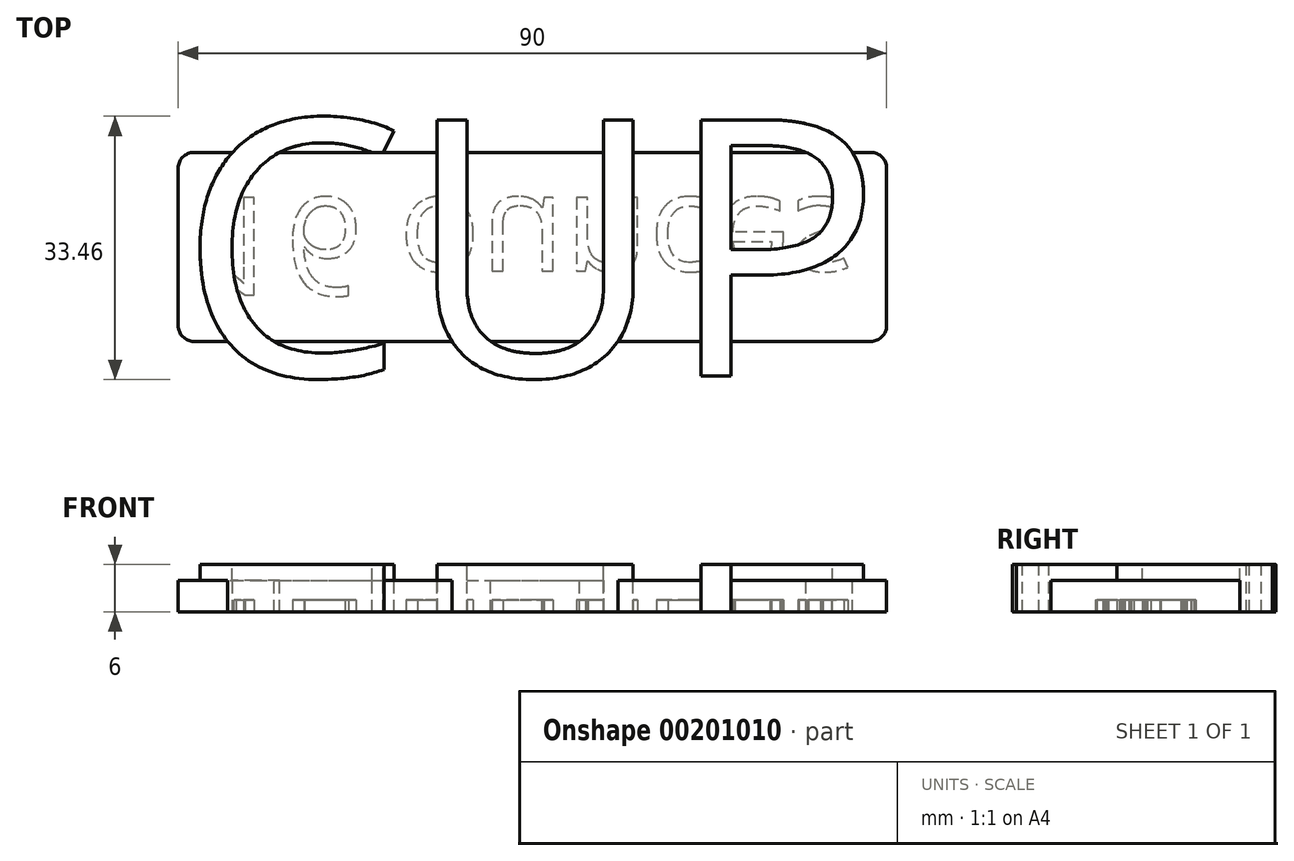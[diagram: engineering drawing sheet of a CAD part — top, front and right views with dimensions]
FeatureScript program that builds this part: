
annotation { "Feature Type Name" : "Feature", "Feature Type Description" : "" }
export const myFeature = defineFeature(function(context is Context, id is Id, definition is map)
    precondition{}
    {
        {
            var Q0;
            Q0=qCreatedBy(makeId("Top.planeOp"),FACE);
            var sketch = newSketch(context, id + "F0", { "sketchPlane" : qUnion([Q0])});
            skLineSegment(sketch, "E0.bottom", {"start": v(-45, 12) * mm, "end": v(45, 12) * mm});
            skLineSegment(sketch, "E0.top", {"start": v(-45, -12) * mm, "end": v(45, -12) * mm});
            skLineSegment(sketch, "E0.left", {"start": v(-45, 12) * mm, "end": v(-45, -12) * mm});
            skLineSegment(sketch, "E0.right", {"start": v(45, 12) * mm, "end": v(45, -12) * mm});
            skLineSegment(sketch, "E1", {"start": v(0, -12) * mm, "end": v(0, 12) * mm, "construction": true});
            skSolve(sketch);
        }
        {
            var Q0;
            Q0=makeQuery(id+"F0.imprint","IMPRINT",FACE,{"disambiguationData":[TD([[makeQuery(id+"F0.imprint","IMPRINT",EDGE,{"derivedFrom":sQuery(id+"F0.wireOp",EDGE,"E0.bottom")}),-1.0]])]});
            extrude(context, id + "F1", {"entities" : qUnion([Q0]), "depth" : 4 * mm});
        }
        {
            var Q0;
            Q0=makeQuery(id+"F1.opExtrude","SWEPT_EDGE",EDGE,{"disambiguationData":[OSD([sQuery(id+"F0.wireOp",EDGE,"E0.top"),sQuery(id+"F0.wireOp",EDGE,"E0.left")])]});
            var Q1;
            Q1=makeQuery(id+"F1.opExtrude","SWEPT_EDGE",EDGE,{"disambiguationData":[OSD([sQuery(id+"F0.wireOp",EDGE,"E0.bottom"),sQuery(id+"F0.wireOp",EDGE,"E0.right")])]});
            var Q2;
            Q2=makeQuery(id+"F1.opExtrude","SWEPT_EDGE",EDGE,{"disambiguationData":[OSD([sQuery(id+"F0.wireOp",EDGE,"E0.bottom"),sQuery(id+"F0.wireOp",EDGE,"E0.left")])]});
            var Q3;
            Q3=makeQuery(id+"F1.opExtrude","SWEPT_EDGE",EDGE,{"disambiguationData":[OSD([sQuery(id+"F0.wireOp",EDGE,"E0.top"),sQuery(id+"F0.wireOp",EDGE,"E0.right")])]});
            fillet(context, id + "F2", {"entities" : qUnion([Q0, Q1, Q2, Q3]), "radius" : 2 * mm, "tangentPropagation" : true, "allowEdgeOverflow" : false});
        }
        {
            var Q0;
            Q0=makeQuery(id+"F1.opExtrude","CAP_FACE",FACE,{"disambiguationData":[OSD([sQuery(id+"F0.wireOp",EDGE,"E0.bottom"),sQuery(id+"F0.wireOp",EDGE,"E0.top"),sQuery(id+"F0.wireOp",EDGE,"E0.left"),sQuery(id+"F0.wireOp",EDGE,"E0.right")])],"isStart":false});
            var sketch = newSketch(context, id + "F3", { "sketchPlane" : qUnion([Q0])});
            skText(sketch, "E2", { "text": "CUP", "fontName": "OpenSans-Regular.ttf"});
            const initialGuessF3  = {"E2": [-0.045, -0.0164, 1, 0, 0.03282]};
            skSetInitialGuess(sketch, initialGuessF3);
            skSolve(sketch);
        }
        {
            var Q0;
            Q0=makeQuery(id+"F1.opExtrude","CAP_FACE",FACE,{"disambiguationData":[OSD([sQuery(id+"F0.wireOp",EDGE,"E0.bottom"),sQuery(id+"F0.wireOp",EDGE,"E0.top"),sQuery(id+"F0.wireOp",EDGE,"E0.left"),sQuery(id+"F0.wireOp",EDGE,"E0.right")])],"isStart":true});
            var sketch = newSketch(context, id + "F4", { "sketchPlane" : qUnion([Q0])});
            skText(sketch, "E3", { "text": "16 ounces", "fontName": "OpenSans-Regular.ttf"});
            const initialGuessF4  = {"E3": [-0.04139, -0.00625, 1, 0, 0.0125]};
            skSetInitialGuess(sketch, initialGuessF4);
            skSolve(sketch);
        }
        {
            var Q0;
            Q0=makeQuery(id+"F4.imprint","IMPRINT",FACE,{"disambiguationData":[TD([[makeQuery(id+"F4.imprint","IMPRINT",EDGE,{"derivedFrom":sQuery(id+"F4.wireOp",EDGE,"E3.sketch_text.stroke-141")}),-1.0]])]});
            var Q1;
            Q1=makeQuery(id+"F4.imprint","IMPRINT",FACE,{"disambiguationData":[TD([[makeQuery(id+"F4.imprint","IMPRINT",EDGE,{"derivedFrom":sQuery(id+"F4.wireOp",EDGE,"E3.sketch_text.stroke-122")}),-1.0]])]});
            var Q2;
            Q2=makeQuery(id+"F4.imprint","IMPRINT",FACE,{"disambiguationData":[TD([[makeQuery(id+"F4.imprint","IMPRINT",EDGE,{"derivedFrom":sQuery(id+"F4.wireOp",EDGE,"E3.sketch_text.stroke-103")}),-1.0]])]});
            var Q3;
            Q3=makeQuery(id+"F4.imprint","IMPRINT",FACE,{"disambiguationData":[TD([[makeQuery(id+"F4.imprint","IMPRINT",EDGE,{"derivedFrom":sQuery(id+"F4.wireOp",EDGE,"E3.sketch_text.stroke-86")}),-1.0]])]});
            var Q4;
            Q4=makeQuery(id+"F4.imprint","IMPRINT",FACE,{"disambiguationData":[TD([[makeQuery(id+"F4.imprint","IMPRINT",EDGE,{"derivedFrom":sQuery(id+"F4.wireOp",EDGE,"E3.sketch_text.stroke-70")}),-1.0]])]});
            var Q5;
            Q5=makeQuery(id+"F4.imprint","IMPRINT",FACE,{"disambiguationData":[TD([[makeQuery(id+"F4.imprint","IMPRINT",EDGE,{"derivedFrom":sQuery(id+"F4.wireOp",EDGE,"E3.sketch_text.stroke-39")}),-1.0]])]});
            var Q6;
            Q6=makeQuery(id+"F4.imprint","IMPRINT",FACE,{"disambiguationData":[TD([[makeQuery(id+"F4.imprint","IMPRINT",EDGE,{"derivedFrom":sQuery(id+"F4.wireOp",EDGE,"E3.sketch_text.stroke-19")}),-1.0]])]});
            var Q7;
            Q7=makeQuery(id+"F4.imprint","IMPRINT",FACE,{"disambiguationData":[TD([[makeQuery(id+"F4.imprint","IMPRINT",EDGE,{"derivedFrom":sQuery(id+"F4.wireOp",EDGE,"E3.sketch_text.stroke-0")}),-1.0]])]});
            var Q8;
            Q8=makeQuery(id+"F4.imprint","IMPRINT",FACE,{"disambiguationData":[TD([[makeQuery(id+"F4.imprint","IMPRINT",EDGE,{"derivedFrom":sQuery(id+"F4.wireOp",EDGE,"E3.sketch_text.stroke-51")}),-1.0]])]});
            extrude(context, id + "F5", {"entities" : qUnion([Q0, Q1, Q2, Q3, Q4, Q5, Q6, Q7, Q8]), "operationType" : NewBodyOperationType.REMOVE, "oppositeDirection" : true, "depth" : 1.5 * mm});
        }
        {
            var Q0;
            {var subQ0=sQuery(id+"F3.wireOp",EDGE,"E2.sketch_text.stroke-4");Q0=makeQuery(id+"F3.imprint","IMPRINT",FACE,{"disambiguationData":[TD([[makeQuery(id+"F3.imprint","IMPRINT",EDGE,{"derivedFrom":subQ0}),-1.0]])]});}
            var Q1;
            {var subQ1=sQuery(id+"F3.wireOp",EDGE,"E2.sketch_text.stroke-1");Q1=makeQuery(id+"F3.imprint","IMPRINT",FACE,{"disambiguationData":[TD([[makeQuery(id+"F3.imprint","IMPRINT",EDGE,{"derivedFrom":subQ1}),-1.0]])]});}
            var Q2;
            {var subQ0=sQuery(id+"F3.wireOp",EDGE,"E2.sketch_text.stroke-11");Q2=makeQuery(id+"F3.imprint","IMPRINT",FACE,{"disambiguationData":[TD([[makeQuery(id+"F3.imprint","IMPRINT",EDGE,{"derivedFrom":subQ0}),-1.0]])]});}
            var Q3;
            {var subQ4=sQuery(id+"F3.wireOp",EDGE,"E2.sketch_text.stroke-17");Q3=makeQuery(id+"F3.imprint","IMPRINT",FACE,{"disambiguationData":[TD([[makeQuery(id+"F3.imprint","IMPRINT",EDGE,{"derivedFrom":subQ4}),-1.0]])]});}
            var Q4;
            {var subQ0=sQuery(id+"F3.wireOp",EDGE,"E2.sketch_text.stroke-23");Q4=makeQuery(id+"F3.imprint","IMPRINT",FACE,{"disambiguationData":[TD([[makeQuery(id+"F3.imprint","IMPRINT",EDGE,{"derivedFrom":subQ0}),-1.0]])]});}
            var Q5;
            {var subQ0=sQuery(id+"F3.wireOp",EDGE,"E2.sketch_text.stroke-26");Q5=makeQuery(id+"F3.imprint","IMPRINT",FACE,{"disambiguationData":[TD([[makeQuery(id+"F3.imprint","IMPRINT",EDGE,{"derivedFrom":subQ0}),-1.0]])]});}
            var Q6;
            {var subQ0=sQuery(id+"F3.wireOp",EDGE,"E2.sketch_text.stroke-21");Q6=makeQuery(id+"F3.imprint","IMPRINT",FACE,{"disambiguationData":[TD([[makeQuery(id+"F3.imprint","IMPRINT",EDGE,{"derivedFrom":subQ0}),-1.0]])]});}
            var Q7;
            {var subQ0=sQuery(id+"F3.wireOp",EDGE,"E2.sketch_text.stroke-28");Q7=makeQuery(id+"F3.imprint","IMPRINT",FACE,{"disambiguationData":[TD([[makeQuery(id+"F3.imprint","IMPRINT",EDGE,{"derivedFrom":subQ0}),-1.0]])]});}
            var Q8;
            {var subQ0=sQuery(id+"F3.wireOp",EDGE,"E2.sketch_text.stroke-33");Q8=makeQuery(id+"F3.imprint","IMPRINT",FACE,{"disambiguationData":[TD([[makeQuery(id+"F3.imprint","IMPRINT",EDGE,{"derivedFrom":subQ0}),-1.0]])]});}
            var Q9;
            {var subQ7=sQuery(id+"F3.wireOp",EDGE,"E2.sketch_text.stroke-29");Q9=makeQuery(id+"F3.imprint","IMPRINT",FACE,{"disambiguationData":[TD([[makeQuery(id+"F3.imprint","IMPRINT",EDGE,{"derivedFrom":subQ7}),-1.0]])]});}
            var Q10;
            {var subQ5=sQuery(id+"F3.wireOp",EDGE,"E2.sketch_text.stroke-35");Q10=makeQuery(id+"F3.imprint","IMPRINT",FACE,{"disambiguationData":[TD([[makeQuery(id+"F3.imprint","IMPRINT",EDGE,{"derivedFrom":subQ5}),-1.0]])]});}
            extrude(context, id + "F6", {"entities" : qUnion([Q0, Q1, Q2, Q3, Q4, Q5, Q6, Q7, Q8, Q9, Q10]), "operationType" : NewBodyOperationType.ADD, "oppositeDirection" : true, "depth" : 4 * mm, "hasSecondDirection" : true, "secondDirectionOppositeDirection" : false, "secondDirectionDepth" : 2 * mm});
        }
    });
